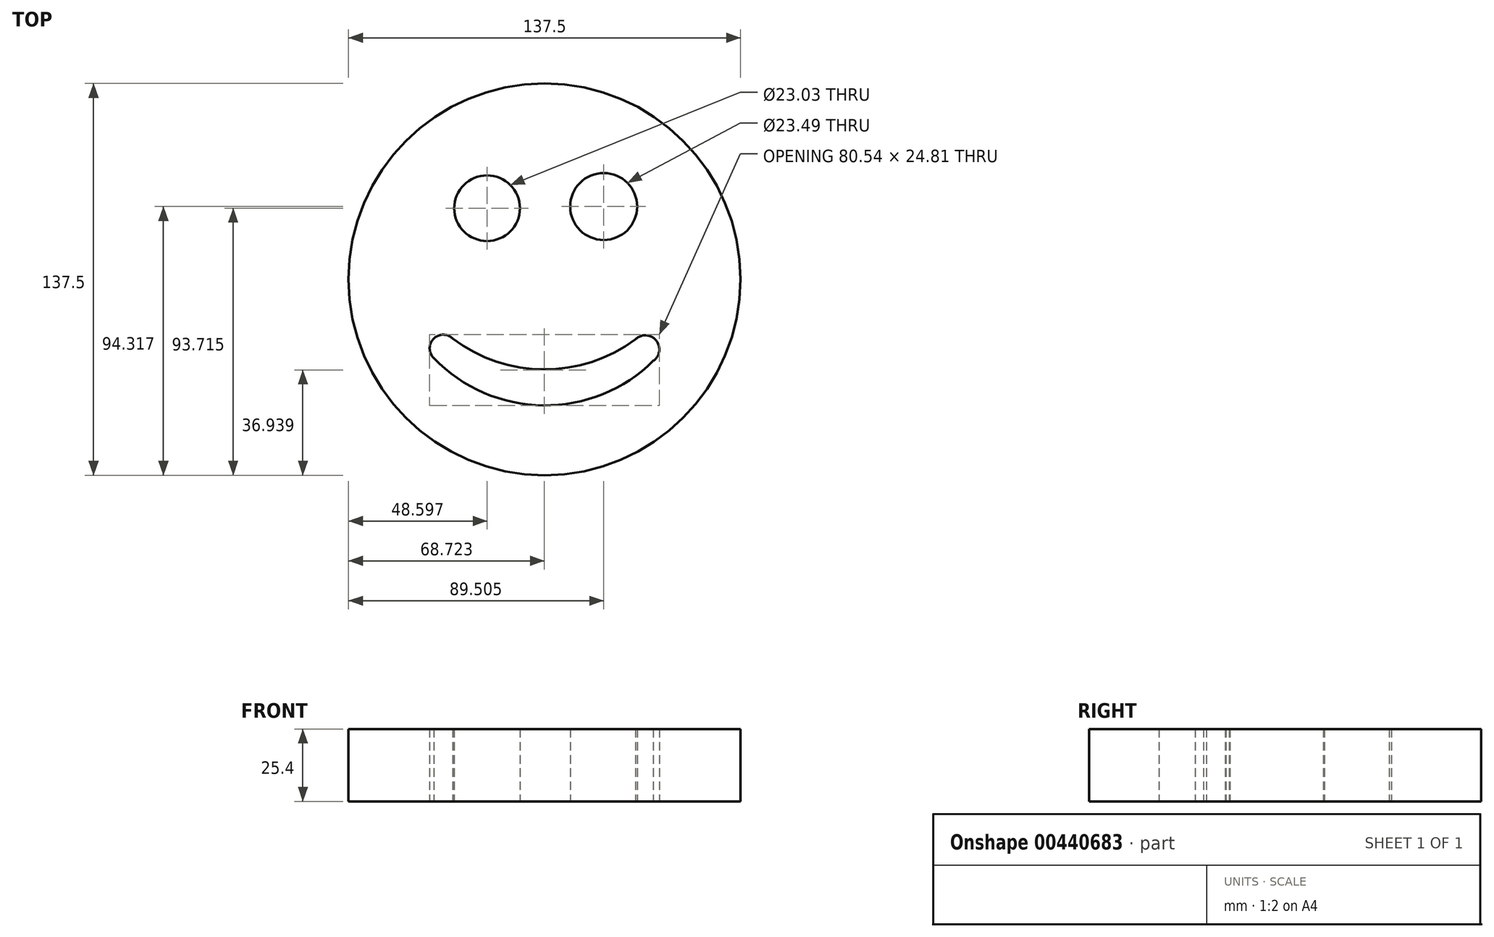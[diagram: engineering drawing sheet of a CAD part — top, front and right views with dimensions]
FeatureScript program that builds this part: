
annotation { "Feature Type Name" : "Feature", "Feature Type Description" : "" }
export const myFeature = defineFeature(function(context is Context, id is Id, definition is map)
    precondition{}
    {
        {
            var Q0;
            Q0=qCreatedBy(makeId("Top.planeOp"),FACE);
            var sketch = newSketch(context, id + "F0", { "sketchPlane" : qUnion([Q0])});
            skCircle(sketch, "E0", {"center": v(0, 0) * mm, "radius": 68.75 * mm});
            skArc(sketch, "E1", {"start": v(-38.8, -27.67) * mm, "mid": v(-0.49, -44.21) * mm, "end": v(38.2, -28.58) * mm});
            skArc(sketch, "E2", {"start": v(-32.18, -20.75) * mm, "mid": v(-0.2, -31.6) * mm, "end": v(31.88, -21.06) * mm});
            skArc(sketch, "E3", {"start": v(-32.18, -20.75) * mm, "mid": v(-38.97, -20.89) * mm, "end": v(-38.8, -27.67) * mm});
            skArc(sketch, "E4", {"start": v(38.2, -28.58) * mm, "mid": v(39.13, -21.38) * mm, "end": v(31.88, -21.06) * mm});
            skCircle(sketch, "E5", {"center": v(-20.15, 24.97) * mm, "radius": 11.51 * mm});
            skCircle(sketch, "E6", {"center": v(20.75, 25.57) * mm, "radius": 11.75 * mm});
            skSolve(sketch);
        }
        {
            var Q0;
            Q0 = qSketchRegion(id + "F0", true);
            extrude(context, id + "F1", {"entities" : qUnion([Q0]), "depth" : 25.4 * mm});
        }
    });
